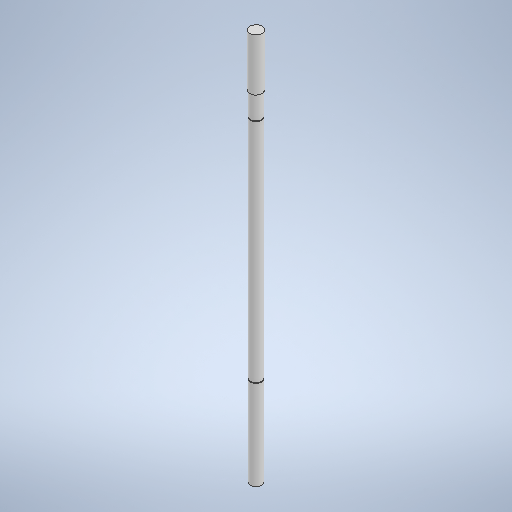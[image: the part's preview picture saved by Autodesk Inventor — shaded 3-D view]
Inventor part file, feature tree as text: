
AUTODESK INVENTOR PART (.ipt)
format: ipt  version: 2025 (Build 290162010, 162A)  size: 276,480 bytes
history: native  units: mm
features: revolve x1, sketch x1
ambient origin geometry x8: Origin, YZ Plane, XZ Plane, XY Plane, X Axis, Y Axis, Z Axis, Center Point
bodies: Solid1 (feature_tree)
feature tree (2):
  revolve  "Revolution1"  [1 undecoded]
  sketch  "Sketch1"  dims[d0=600.0mm d1=8.5mm d2=1.0mm d3=1.0mm d4=115.0mm d5=360.0deg d6=1.0mm d7=1.0mm d8=462.0mm d11=1.0mm d12=80.0mm]
note: 1 required parameter value undecoded (feature->parameter linkage not recoverable at this tier; creation-order binding heuristic only, values carry confidence <= 0.55)
